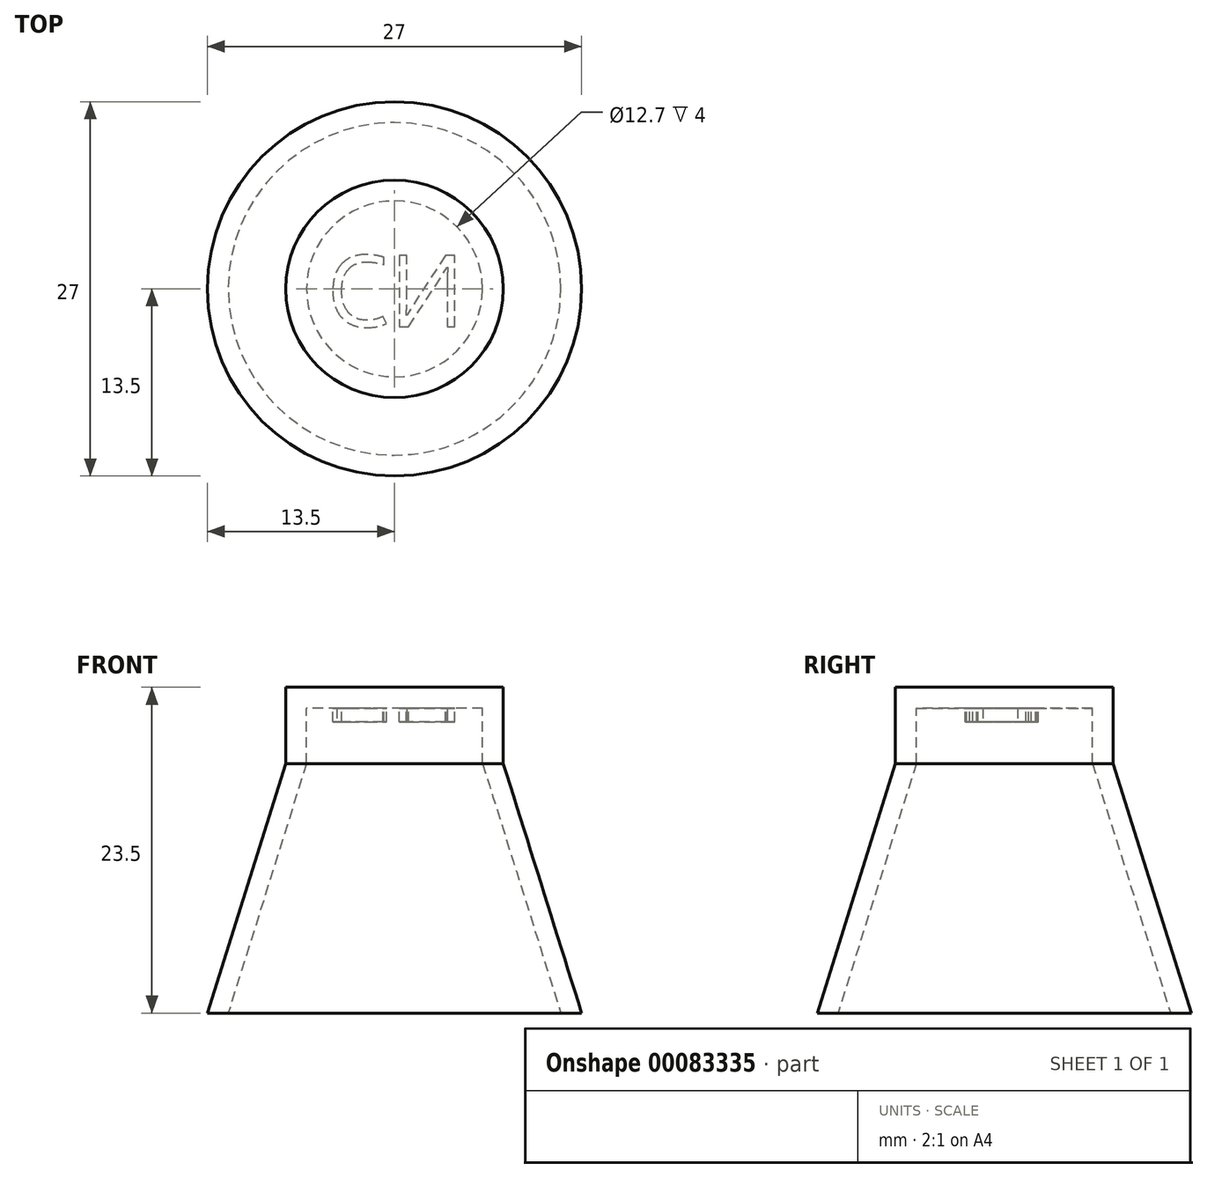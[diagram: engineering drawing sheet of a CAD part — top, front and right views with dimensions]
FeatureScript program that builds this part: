
annotation { "Feature Type Name" : "Feature", "Feature Type Description" : "" }
export const myFeature = defineFeature(function(context is Context, id is Id, definition is map)
    precondition{}
    {
        {
            var Q0;
            Q0=qCreatedBy(makeId("Front.planeOp"),FACE);
            var sketch = newSketch(context, id + "F0", { "sketchPlane" : qUnion([Q0])});
            skLineSegment(sketch, "E0", {"start": v(0, 0) * mm, "end": v(6.35, 0) * mm});
            skLineSegment(sketch, "E1", {"start": v(6.35, 0) * mm, "end": v(6.35, -4) * mm});
            skLineSegment(sketch, "E2", {"start": v(0, 0) * mm, "end": v(0, -22) * mm, "construction": true});
            skLineSegment(sketch, "E3", {"start": v(0, -22) * mm, "end": v(12, -22) * mm, "construction": true});
            skLineSegment(sketch, "E4", {"start": v(12, -22) * mm, "end": v(6.35, -4) * mm, "construction": true});
            skLineSegment(sketch, "E5", {"start": v(0, 0) * mm, "end": v(0, -22) * mm});
            skLineSegment(sketch, "E6", {"start": v(12, -22) * mm, "end": v(6.35, -4) * mm});
            skLineSegment(sketch, "E7", {"start": v(0, -22) * mm, "end": v(12, -22) * mm});
            skLineSegment(sketch, "E8", {"start": v(0, 0) * mm, "end": v(0, 1.5) * mm});
            skLineSegment(sketch, "E9", {"start": v(0, 1.5) * mm, "end": v(7.85, 1.5) * mm});
            skLineSegment(sketch, "E10", {"start": v(7.85, 1.5) * mm, "end": v(7.85, -4) * mm});
            skLineSegment(sketch, "E11", {"start": v(7.85, -4) * mm, "end": v(13.5, -22) * mm});
            skLineSegment(sketch, "E12", {"start": v(13.5, -22) * mm, "end": v(12, -22) * mm});
            skLineSegment(sketch, "E13", {"start": v(6.35, -4) * mm, "end": v(7.85, -4) * mm});
            skSolve(sketch);
        }
        {
            var Q0;
            Q0=makeQuery(id+"F0.imprint","IMPRINT",FACE,{"disambiguationData":[TD([[makeQuery(id+"F0.imprint","IMPRINT",EDGE,{"derivedFrom":sQuery(id+"F0.wireOp",EDGE,"E0")}),1.0]])]});
            var Q1;
            Q1=makeQuery(id+"F0.imprint","IMPRINT",FACE,{"disambiguationData":[TD([[makeQuery(id+"F0.imprint","IMPRINT",EDGE,{"derivedFrom":sQuery(id+"F0.wireOp",EDGE,"E6")}),-1.0]])]});
            var Q2;
            Q2=sQuery(id+"F0.wireOp",EDGE,"E5");
            revolve(context, id + "F1", {"entities" : qUnion([Q0, Q1]), "axis" : qUnion([Q2]), "revolveType" : RevolveType.FULL});
        }
        {
            var Q0;
            Q0=makeQuery(id+"F1.opRevolve","SWEPT_FACE",FACE,{"disambiguationData":[OSD([sQuery(id+"F0.wireOp",EDGE,"E0")])]});
            var sketch = newSketch(context, id + "F2", { "sketchPlane" : qUnion([Q0])});
            skText(sketch, "E14", { "text": "CN", "fontName": "OpenSans-Regular.ttf"});
            const initialGuessF2  = {"E14": [-0.00489, -0.0024, 1, 0, 0.00517]};
            skSetInitialGuess(sketch, initialGuessF2);
            skSolve(sketch);
        }
        {
            var Q0;
            Q0 = qSketchRegion(id + "F2", true);
            extrude(context, id + "F3", {"entities" : qUnion([Q0]), "operationType" : NewBodyOperationType.ADD, "depth" : 1 * mm});
        }
    });
